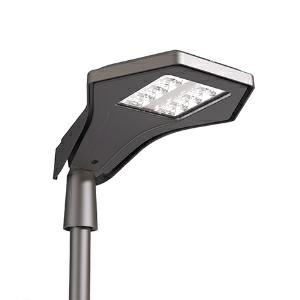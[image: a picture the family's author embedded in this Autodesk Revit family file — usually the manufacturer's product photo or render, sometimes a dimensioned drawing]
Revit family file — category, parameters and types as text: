
# Revit family: 3f_filippi_-_3f_manta_ampio_3f_filippi_-_7001_-_3f_manta_an_50-730_wide
name_source: partatom
category: Lighting Fixtures
units: mm (PartAtom-declared; Revit-internal decimal feet)

## family parameters
Cut with Voids When Loaded = No
Host = Face
Light Source = No
Part Type = Normal
Room Calculation Point = No
Round Connector Dimension = Use Diameter
Shared = No

## types (1)
- 3F Filippi - 3F Manta Ampio (1 x LED, 6950 lm, 53 W, 3000 K)
    Apparent Load = 53 VA
    Approval mark = CE
    CIE Flux Codes = 37 75 99 100 100
    Color Rendering = 70
    Color Temperature = 3000 K
    Control Gear = Electronic ballast
    Default Elevation = 1800 mm
    Description = ILLUMINOTECHNICAL
Luminous efficiency 100% (DLOR 100%, ULOR 0%).
Initial luminous flux of the luminaire 6950 lm.
Asymmetric distribution with wide bilateral.
BUG (Backlight, Uplight, Glare) IESNA TM-15: B2 U0 G1.
Luminous efficacy 131 lm/W.
Lifetime (L93/B10): 30000 h. (tq+25°C)
Lifetime (L90/B10): 50000 h. (tq+25°C)
Lifetime (L85/B10): 80000 h. (tq+25°C)
Lifetime (L80/B10): 100000 h. (tq+25°C)
Lifetime (L90/B20): 50000 h. (tq+50°C)
Sudden decreased luminous flux after 50000 hours: 0% (C0).
Photobiological safety in compliance with IEC/TR 62778: RG0 risk exempt, (IEC 62471).
In compliance with IEC/EN 62722-2-1 - IEC/EN 62717 standards.

SOURCE
Squared LED module 50W/730.
Source with special protection against aggressive chemically-volatile substances for standard LED technology.
Energy efficiency class (UE 2019/2020 - UE 2019/2015): D.
CIE 13.3 Colour rendering index: CRI >70 (R9 <50%).
IES TM-30 Fidelity Index: Rf = 72 Rg = 95.
CCT nominal colour temperature 3000 K.
Colour initial tolerance (MacAdam): SDCM 5.

MECHANICAL
Aerodynamically-shaped die-cast aluminium double-shell body for low wind resistance (frontal: 0.0446 m²; lateral: 0.0505 m²), equipped with fins to optimize the cooling of the internal components.
Shell closure using stainless steel screws on stainless steel bushings, with hinged opening for easy access to the wiring compartment, equipped with system against accidental closure.
Polyester powder coating with degreasing pre-treatment and phosphate layer deposit on the metal, UV stabilised, corrosion resistant, anthracite colour, salt spray resistance ISO 9227 >1000 h.
Parabolic cellular optics with total recovery, entirely made of semi-specular high reflection aluminium with titanium and magnesium surface treatment, to maintain optical performance over time.
Polyurethane foam seals, ecological, anti-aging, installed using a continuous automatic process with no joints.
VT extra transparent tempered glass diffuser, 4 mm thick, non-combustible, with Heat Soak Test (HST) thermal treatment, which drastically reduces the risk of spontaneous breakage.
Stainless steel internal and external screws.
Luminaire with limited surface temperature. - D - (EN 60598-2-24)
Dimensions: 660x440 mm, height 166 mm. Weight 10.37 kg.
IP66 protection degree.
Mechanical strength to impacts IK08 (5 joule).
Glow-wire test resistance 960°C.

ELECTRICAL
Halogen Free electronic wiring 230V-50/60Hz, power factor 0.97, THD <25%, constant output current, class I, 1 driver.
Power of the luminaire 53 W.
ENEC - CE.
SAFE FLICKER: PstLM=<1 and SVM=<0.4 (IEC TR 61547-1 and IEC TR 63158), to ensure a more comfortable and safe light.
Ambient temperature from -20°C to +50°C.
Temperature class T6 max 85°C.
Safety break switch to shut off the power supply when opening the device.
Insulation voltage 6kV via Sourge Protector.
SPD type 2+3 (combined) device to protect against voltage surges up to 10 kV in common and differential mode.
Thermal protection of the LED module via NTC sensor (Negative Temperature Coefficient).
M20x1.5 IP68 nylon cable gland for feeding input (cables with an min-max diameter 6-13mm).
Pressure compensating valve with anti-condensation effect.
Relative humidity UR: <85%.

INSTALLATION
Post-top / arm / wall.
Installation with always necessary "Pole fixing" accessory (see accessories).
All accessories dedicated to this product are available on the Catalog and on our website www.3F-Filippi.com.

ACCESSORIES
Pole mount in die-cast aluminium with the same paint treatment as the body (for Ø 60 mm and Ø 76 mm poles) equipped with special teeth for adjusting the inclination on the head of the device by ± 20° with an adjustment pitch of 5°.
Possibility of installing on vertical pole (pole head) and horizontal pole (arm).
Mounting on the device using the supplied stainless steel screws on self-locking stainless steel nuts.
A0439 - Pole mounting diameter 60 mm.
A0440 - Pole mounting diameter 76 mm.

APPLICATIONS
Outdoor environments, general lighting, work and roadway lighting, transit areas and building perimeters, parking lots, trade fairs.
Control of light pollution, in accordance with the legislative requirements in force.

LIGHT MANAGEMENT
Upon request, the appliance can be supplied with "Virtual Midnight" programming.

WARNING
Luminaire designed for disposal/recycling at end-of-life.
Replaceable (LED only) light source by a professional. Replaceable control gear by a professional.
    Height = 166 mm
    Lamp = 1 x LED
    Lamp Light Flux = 6950 lm
    Lamp Power = 53 W
    Lamp count = 1
    Length = 660 mm
    Lifetime = 50000 h
    Luminous efficacy = 131 lm/W
    Manufacturer = 3F Filippi
    ModVariant = No
    Model = 3F Filippi - 7001 - 3F Manta AN 50-730 WIDE
    Mounting Place = Pole
    Mounting Type = Pole top
    Number of Poles = 1
    OnlyDefault = Yes
    Power Factor = 1
    Product Name = 3F Filippi - 3F Manta Ampio
    Product group = street luminaire
    ProductGroupID = 15
    Protection Class = Protection class I
    Protection Degree = IP 66
    RLX_Detail_Level = 1
    RLX_Emergency_Light_Flux = 0 lm
    RLX_Emergency_Type = 0
    RLX_Emergency_Type_DB = No
    RlxData = <blob elided: 225613 chars, md5=29069136>
    Socket = socket
    Standby Power = 0 W
    System Light Flux = 6950 lm
    System Power = 53 W
    Type Comments = Product without accessories
    Type Image = 3ffilippi_3f_manta_wide.jpg
    URL = http://relux.com
    VarID = ---
    Voltage = 0 V
    Weight = 0.00 kg
    Width = 440 mm

## geometry (parser evidence)
native form markers: Blend x4, Sweep x14
no freeform markers — native parametric forms only
